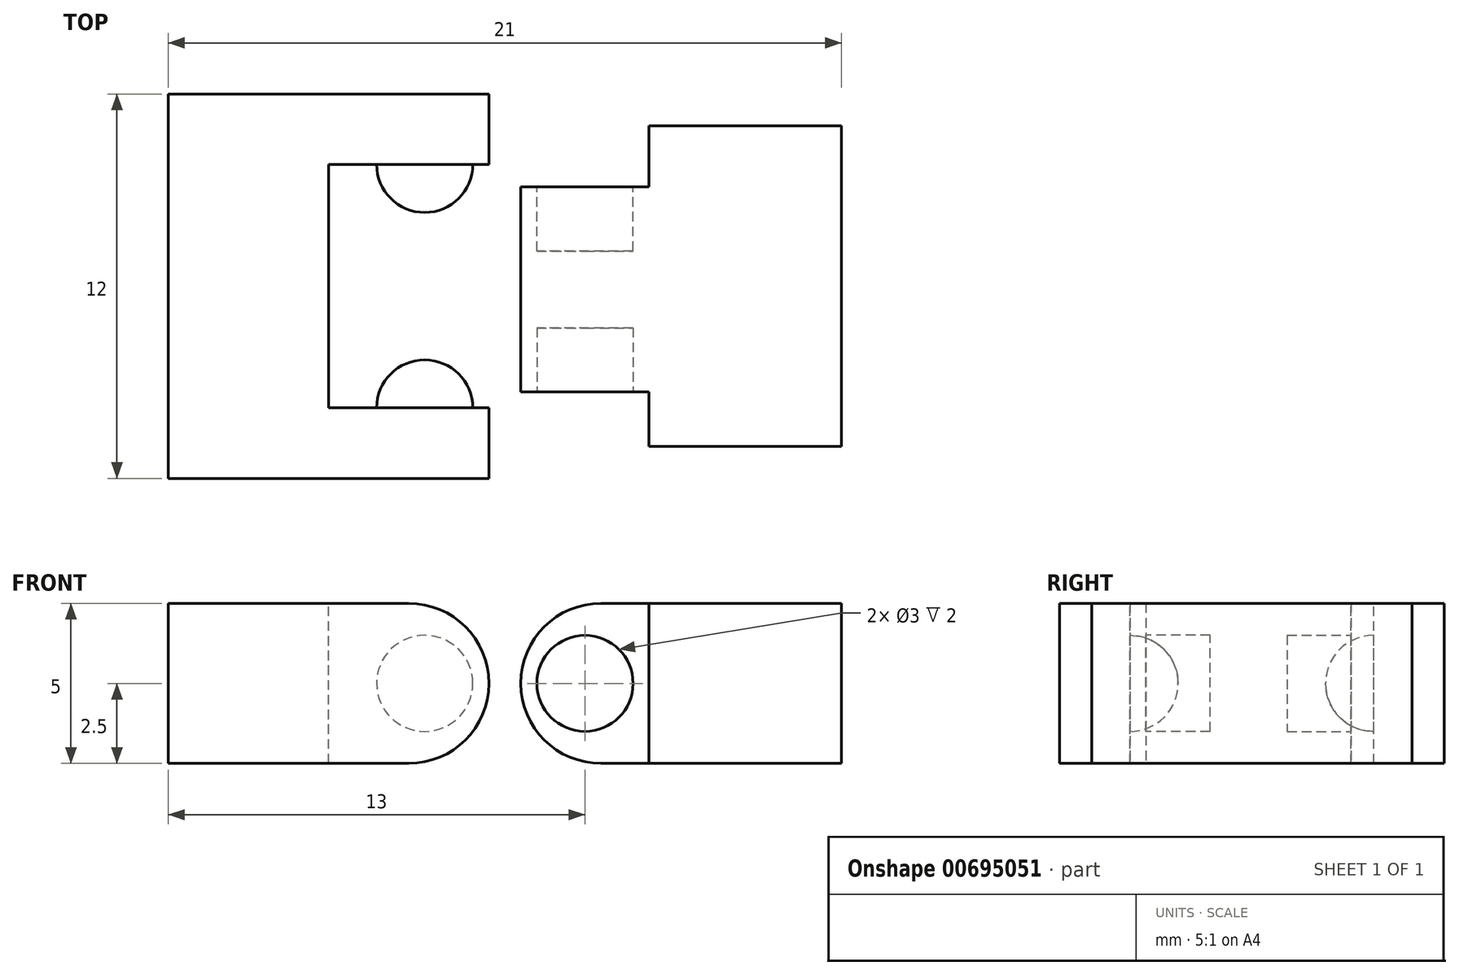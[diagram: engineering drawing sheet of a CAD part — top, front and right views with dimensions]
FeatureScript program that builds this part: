
annotation { "Feature Type Name" : "Feature", "Feature Type Description" : "" }
export const myFeature = defineFeature(function(context is Context, id is Id, definition is map)
    precondition{}
    {
        {
            var Q0;
            Q0=qCreatedBy(makeId("Top.planeOp"),FACE);
            var sketch = newSketch(context, id + "F0", { "sketchPlane" : qUnion([Q0])});
            skLineSegment(sketch, "E0", {"start": v(0, 0) * mm, "end": v(0, 6.4) * mm});
            skLineSegment(sketch, "E1", {"start": v(0, 6.4) * mm, "end": v(4, 6.4) * mm});
            skLineSegment(sketch, "E2", {"start": v(4, 6.4) * mm, "end": v(4, 8.3) * mm});
            skLineSegment(sketch, "E3", {"start": v(4, 8.3) * mm, "end": v(8, 8.3) * mm});
            skLineSegment(sketch, "E4", {"start": v(8, 8.3) * mm, "end": v(8, -1.7) * mm});
            skLineSegment(sketch, "E5", {"start": v(8, -1.7) * mm, "end": v(4, -1.7) * mm});
            skLineSegment(sketch, "E6", {"start": v(4, -1.7) * mm, "end": v(4, 0) * mm});
            skLineSegment(sketch, "E7", {"start": v(4, 0) * mm, "end": v(0, 0) * mm});
            skLineSegment(sketch, "E8", {"start": v(-1, 7.1) * mm, "end": v(-5, 7.1) * mm});
            skLineSegment(sketch, "E9", {"start": v(-5, 7.1) * mm, "end": v(-5, -0.5) * mm});
            skLineSegment(sketch, "E10", {"start": v(-5, -0.5) * mm, "end": v(-1, -0.5) * mm});
            skLineSegment(sketch, "E11", {"start": v(-1, -0.5) * mm, "end": v(-1, -1.7) * mm});
            skLineSegment(sketch, "E12", {"start": v(-1, -1.7) * mm, "end": v(-9, -1.7) * mm});
            skLineSegment(sketch, "E13", {"start": v(-9, -1.7) * mm, "end": v(-9, 8.3) * mm});
            skLineSegment(sketch, "E14", {"start": v(-9, 8.3) * mm, "end": v(-1, 8.3) * mm});
            skLineSegment(sketch, "E15", {"start": v(-1, 8.3) * mm, "end": v(-1, 7.1) * mm});
            skSolve(sketch);
        }
        {
            var Q0;
            Q0=makeQuery(id+"F0.imprint","IMPRINT",FACE,{"disambiguationData":[TD([[makeQuery(id+"F0.imprint","IMPRINT",EDGE,{"derivedFrom":sQuery(id+"F0.wireOp",EDGE,"E0")}),-1.0]])]});
            var Q1;
            Q1=makeQuery(id+"F0.imprint","IMPRINT",FACE,{"disambiguationData":[TD([[makeQuery(id+"F0.imprint","IMPRINT",EDGE,{"derivedFrom":sQuery(id+"F0.wireOp",EDGE,"E8")}),-1.0]])]});
            extrude(context, id + "F1", {"entities" : qUnion([Q0, Q1]), "depth" : 5 * mm, "offsetDistance" : 25 * mm});
        }
        {
            var Q0;
            Q0=makeQuery(id+"F1.opExtrude","SWEPT_FACE",FACE,{"disambiguationData":[OSD([sQuery(id+"F0.wireOp",EDGE,"E8")])]});
            var sketch = newSketch(context, id + "F2", { "sketchPlane" : qUnion([Q0])});
            skLineSegment(sketch, "E16", {"start": v(-1, 5) * mm, "end": v(-5, 0) * mm, "construction": true});
            skCircle(sketch, "E17", {"center": v(-3, 2.5) * mm, "radius": 1.5 * mm});
            skSolve(sketch);
        }
        {
            var Q0;
            Q0=makeQuery(id+"F2.imprint","IMPRINT",FACE,{"disambiguationData":[TD([[makeQuery(id+"F2.imprint","IMPRINT",EDGE,{"derivedFrom":sQuery(id+"F2.wireOp",EDGE,"E17")}),1.0]])]});
            var Q1;
            Q1=sQuery(id+"F2.wireOp",EDGE,"E17");
            extrude(context, id + "F3", {"entities" : qUnion([Q0]), "operationType" : NewBodyOperationType.ADD, "surfaceEntities" : qUnion([Q1]), "depth" : 1.5 * mm, "offsetDistance" : 25 * mm});
        }
        {
            var Q0;
            Q0=makeQuery(id+"F1.opExtrude","SWEPT_FACE",FACE,{"disambiguationData":[OSD([sQuery(id+"F0.wireOp",EDGE,"E1")])]});
            var sketch = newSketch(context, id + "F4", { "sketchPlane" : qUnion([Q0])});
            skLineSegment(sketch, "E18", {"start": v(0, 5) * mm, "end": v(-4, 0) * mm, "construction": true});
            skCircle(sketch, "E19", {"center": v(-2, 2.5) * mm, "radius": 1.5 * mm});
            skSolve(sketch);
        }
        {
            var Q0;
            Q0=makeQuery(id+"F4.imprint","IMPRINT",FACE,{"disambiguationData":[TD([[makeQuery(id+"F4.imprint","IMPRINT",EDGE,{"derivedFrom":sQuery(id+"F4.wireOp",EDGE,"E19")}),1.0]])]});
            extrude(context, id + "F5", {"entities" : qUnion([Q0]), "operationType" : NewBodyOperationType.REMOVE, "oppositeDirection" : true, "depth" : 2 * mm, "offsetDistance" : 25 * mm});
        }
        {
            var Q0;
            Q0=makeQuery(id+"F1.opExtrude","SWEPT_FACE",FACE,{"disambiguationData":[OSD([sQuery(id+"F0.wireOp",EDGE,"E10")])]});
            var sketch = newSketch(context, id + "F6", { "sketchPlane" : qUnion([Q0])});
            skLineSegment(sketch, "E20", {"start": v(1, 5) * mm, "end": v(5, 0) * mm, "construction": true});
            skCircle(sketch, "E21", {"center": v(3, 2.5) * mm, "radius": 1.5 * mm});
            skSolve(sketch);
        }
        {
            var Q0;
            Q0 = qSketchRegion(id + "F6", true);
            extrude(context, id + "F7", {"entities" : qUnion([Q0]), "operationType" : NewBodyOperationType.ADD, "depth" : 1.5 * mm, "offsetDistance" : 25 * mm});
        }
        {
            var Q0;
            Q0=makeQuery(id+"F7.opExtrude","CAP_EDGE",EDGE,{"disambiguationData":[OSD([sQuery(id+"F6.wireOp",EDGE,"E21")])],"isStart":false});
            var Q1;
            Q1=makeQuery(id+"F3.opExtrude","CAP_EDGE",EDGE,{"disambiguationData":[OSD([sQuery(id+"F2.wireOp",EDGE,"E17")])],"isStart":false});
            fillet(context, id + "F8", {"entities" : qUnion([Q0, Q1]), "radius" : 1.5 * mm, "tangentPropagation" : true, "allowEdgeOverflow" : false});
        }
        {
            var Q0;
            Q0=makeQuery(id+"F1.opExtrude","CAP_FACE",FACE,{"disambiguationData":[OSD([sQuery(id+"F0.wireOp",EDGE,"E8"),sQuery(id+"F0.wireOp",EDGE,"E9"),sQuery(id+"F0.wireOp",EDGE,"E10"),sQuery(id+"F0.wireOp",EDGE,"E11"),sQuery(id+"F0.wireOp",EDGE,"E12"),sQuery(id+"F0.wireOp",EDGE,"E13"),sQuery(id+"F0.wireOp",EDGE,"E14"),sQuery(id+"F0.wireOp",EDGE,"E15")])],"isStart":false});
            var sketch = newSketch(context, id + "F9", { "sketchPlane" : qUnion([Q0])});
            skLineSegment(sketch, "E22.bottom", {"start": v(-5, 7.1) * mm, "end": v(-6, 7.1) * mm});
            skLineSegment(sketch, "E22.top", {"start": v(-5, -0.5) * mm, "end": v(-6, -0.5) * mm});
            skLineSegment(sketch, "E22.left", {"start": v(-5, 7.1) * mm, "end": v(-5, -0.5) * mm});
            skLineSegment(sketch, "E22.right", {"start": v(-6, 7.1) * mm, "end": v(-6, -0.5) * mm});
            skSolve(sketch);
        }
        {
            var Q0;
            Q0 = qSketchRegion(id + "F9", true);
            extrude(context, id + "F10", {"entities" : qUnion([Q0]), "operationType" : NewBodyOperationType.REMOVE, "endBound" : BoundingType.UP_TO_NEXT, "oppositeDirection" : true, "depth" : 25 * mm, "offsetDistance" : 25 * mm});
        }
        {
            var Q0;
            Q0=makeQuery(id+"F1.opExtrude","SWEPT_FACE",FACE,{"disambiguationData":[OSD([sQuery(id+"F0.wireOp",EDGE,"E12")])]});
            extrude(context, id + "F11", {"entities" : qUnion([Q0]), "operationType" : NewBodyOperationType.ADD, "depth" : 1 * mm, "offsetDistance" : 25 * mm});
        }
        {
            var Q0;
            Q0=makeQuery(id+"F1.opExtrude","SWEPT_FACE",FACE,{"disambiguationData":[OSD([sQuery(id+"F0.wireOp",EDGE,"E14")])]});
            extrude(context, id + "F12", {"entities" : qUnion([Q0]), "operationType" : NewBodyOperationType.ADD, "depth" : 1 * mm, "offsetDistance" : 25 * mm});
        }
        {
            var Q0;
            Q0=makeQuery(id+"F1.opExtrude","CAP_EDGE",EDGE,{"disambiguationData":[OSD([sQuery(id+"F0.wireOp",EDGE,"E0")])],"isStart":false});
            var Q1;
            Q1=makeQuery(id+"F1.opExtrude","CAP_EDGE",EDGE,{"disambiguationData":[OSD([sQuery(id+"F0.wireOp",EDGE,"E0")])],"isStart":true});
            var Q2;
            {var subQ0=sQuery(id+"F0.wireOp",EDGE,"E12");var subQ1=sQuery(id+"F0.wireOp",EDGE,"E11");Q2=makeQuery(id+"F11.boolean.opBoolean","MERGE",EDGE,{"derivedFrom":[makeQuery(id+"F1.opExtrude","CAP_EDGE",EDGE,{"disambiguationData":[OSD([subQ1])],"isStart":true}),makeQuery(id+"F11.opExtrude","SWEPT_EDGE",EDGE,{"disambiguationData":[OSD([subQ1,subQ0]),TDD([makeQuery(id+"F1.opExtrude","CAP_VERTEX",VERTEX,{"disambiguationData":[OSD([subQ1,subQ0])],"isStart":true})])]})]});}
            var Q3;
            {var subQ0=sQuery(id+"F0.wireOp",EDGE,"E12");var subQ1=sQuery(id+"F0.wireOp",EDGE,"E11");Q3=makeQuery(id+"F11.boolean.opBoolean","MERGE",EDGE,{"derivedFrom":[makeQuery(id+"F1.opExtrude","CAP_EDGE",EDGE,{"disambiguationData":[OSD([subQ1])],"isStart":false}),makeQuery(id+"F11.opExtrude","SWEPT_EDGE",EDGE,{"disambiguationData":[OSD([subQ1,subQ0]),TDD([makeQuery(id+"F1.opExtrude","CAP_VERTEX",VERTEX,{"disambiguationData":[OSD([subQ1,subQ0])],"isStart":false})])]})]});}
            var Q4;
            {var subQ0=sQuery(id+"F0.wireOp",EDGE,"E15");var subQ1=sQuery(id+"F0.wireOp",EDGE,"E14");Q4=makeQuery(id+"F12.boolean.opBoolean","MERGE",EDGE,{"derivedFrom":[makeQuery(id+"F1.opExtrude","CAP_EDGE",EDGE,{"disambiguationData":[OSD([subQ0])],"isStart":false}),makeQuery(id+"F12.opExtrude","SWEPT_EDGE",EDGE,{"disambiguationData":[OSD([subQ1,subQ0]),TDD([makeQuery(id+"F1.opExtrude","CAP_VERTEX",VERTEX,{"disambiguationData":[OSD([subQ1,subQ0])],"isStart":false})])]})]});}
            var Q5;
            {var subQ0=sQuery(id+"F0.wireOp",EDGE,"E15");var subQ1=sQuery(id+"F0.wireOp",EDGE,"E14");Q5=makeQuery(id+"F12.boolean.opBoolean","MERGE",EDGE,{"derivedFrom":[makeQuery(id+"F1.opExtrude","CAP_EDGE",EDGE,{"disambiguationData":[OSD([subQ0])],"isStart":true}),makeQuery(id+"F12.opExtrude","SWEPT_EDGE",EDGE,{"disambiguationData":[OSD([subQ1,subQ0]),TDD([makeQuery(id+"F1.opExtrude","CAP_VERTEX",VERTEX,{"disambiguationData":[OSD([subQ1,subQ0])],"isStart":true})])]})]});}
            fillet(context, id + "F13", {"entities" : qUnion([Q0, Q1, Q2, Q3, Q4, Q5]), "radius" : 2.5 * mm, "tangentPropagation" : true, "allowEdgeOverflow" : false});
        }
        {
            var Q0;
            Q0=makeQuery(id+"F1.opExtrude","SWEPT_FACE",FACE,{"disambiguationData":[OSD([sQuery(id+"F0.wireOp",EDGE,"E4")])]});
            extrude(context, id + "F14", {"entities" : qUnion([Q0]), "operationType" : NewBodyOperationType.ADD, "depth" : 2 * mm, "offsetDistance" : 25 * mm});
        }
        {
            var Q0;
            {var subQ0=sQuery(id+"F0.wireOp",EDGE,"E13");Q0=makeQuery(id+"F12.boolean.opBoolean","MERGE",FACE,{"derivedFrom":[makeQuery(id+"F11.boolean.opBoolean","MERGE",FACE,{"derivedFrom":[makeQuery(id+"F1.opExtrude","SWEPT_FACE",FACE,{"disambiguationData":[OSD([subQ0])]}),makeQuery(id+"F11.opExtrude","SWEPT_FACE",FACE,{"disambiguationData":[OSD([sQuery(id+"F0.wireOp",EDGE,"E12"),subQ0])]})]}),makeQuery(id+"F12.opExtrude","SWEPT_FACE",FACE,{"disambiguationData":[OSD([subQ0,sQuery(id+"F0.wireOp",EDGE,"E14")])]})]});}
            extrude(context, id + "F15", {"entities" : qUnion([Q0]), "operationType" : NewBodyOperationType.ADD, "depth" : 2 * mm, "offsetDistance" : 25 * mm});
        }
        {
            var Q0;
            Q0=makeQuery(id+"F1.opExtrude","SWEPT_FACE",FACE,{"disambiguationData":[OSD([sQuery(id+"F0.wireOp",EDGE,"E7")])]});
            var sketch = newSketch(context, id + "F16", { "sketchPlane" : qUnion([Q0])});
            skCircle(sketch, "E23.0", {"center": v(2, 2.5) * mm, "radius": 1.5 * mm});
            skSolve(sketch);
        }
        {
            var Q0;
            Q0=makeQuery(id+"F16.imprint","IMPRINT",FACE,{"disambiguationData":[TD([[makeQuery(id+"F16.imprint","IMPRINT",EDGE,{"derivedFrom":sQuery(id+"F16.wireOp",EDGE,"E23.0")}),1.0]])]});
            extrude(context, id + "F17", {"entities" : qUnion([Q0]), "operationType" : NewBodyOperationType.REMOVE, "oppositeDirection" : true, "depth" : 2 * mm, "offsetDistance" : 25 * mm});
        }
    });
